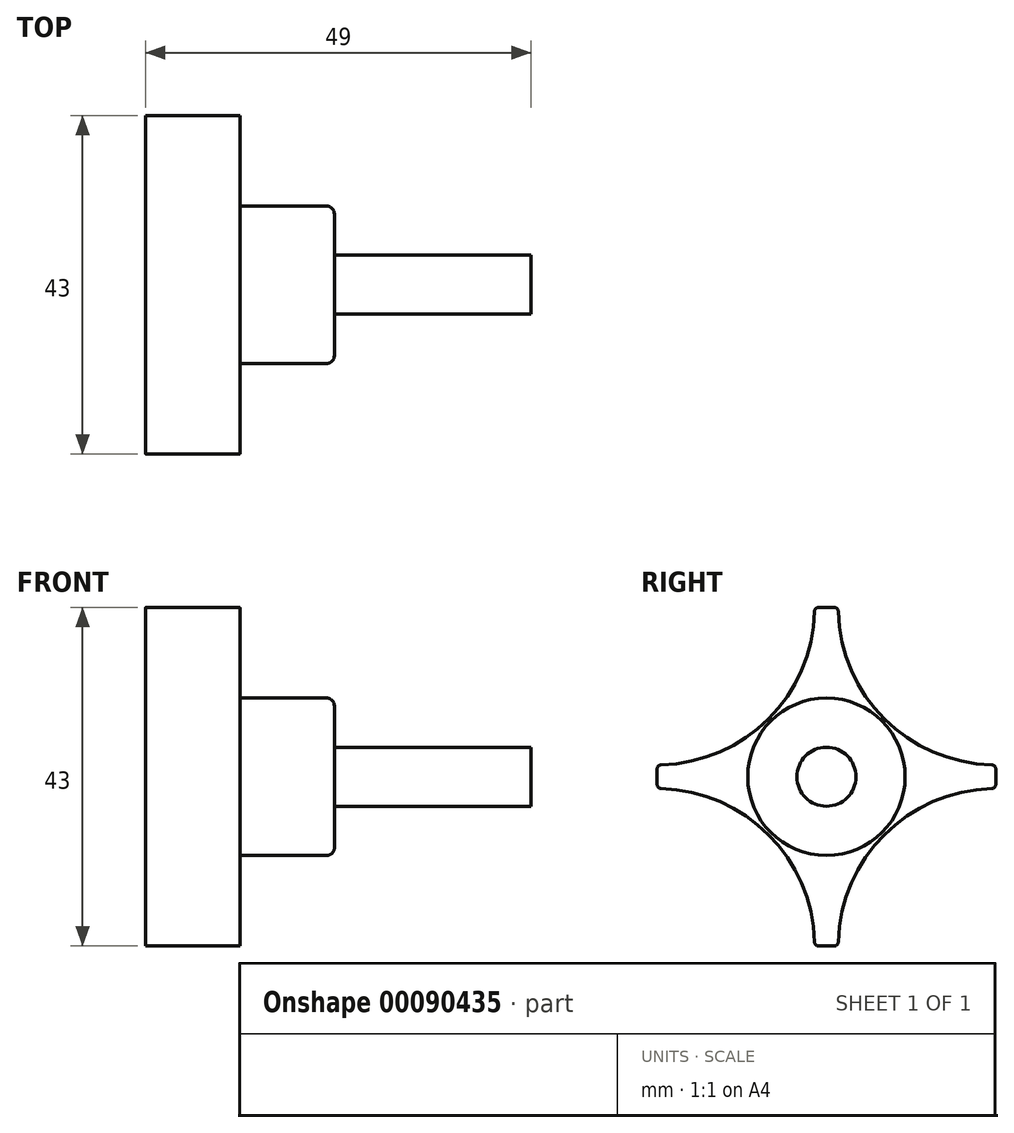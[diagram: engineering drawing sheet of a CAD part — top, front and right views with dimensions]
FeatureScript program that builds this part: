
annotation { "Feature Type Name" : "Feature", "Feature Type Description" : "" }
export const myFeature = defineFeature(function(context is Context, id is Id, definition is map)
    precondition{}
    {
        {
            var Q0;
            Q0=qCreatedBy(makeId("Right.planeOp"),FACE);
            var sketch = newSketch(context, id + "F0", { "sketchPlane" : qUnion([Q0])});
            skLineSegment(sketch, "E0.bottom", {"start": v(1.5, 21.5) * mm, "end": v(-1.5, 21.5) * mm});
            skLineSegment(sketch, "E0.top", {"start": v(1.5, -21.5) * mm, "end": v(-1.5, -21.5) * mm});
            skLineSegment(sketch, "E0.left", {"start": v(21.5, 1.5) * mm, "end": v(21.5, -1.5) * mm});
            skLineSegment(sketch, "E0.right", {"start": v(-21.5, 1.5) * mm, "end": v(-21.5, -1.5) * mm});
            skPoint(sketch, "E0.middle", {"position": v(0, 0) * mm});
            skArc(sketch, "E1", {"start": v(-1.5, 21.5) * mm, "mid": v(-7.36, 7.36) * mm, "end": v(-21.5, 1.5) * mm});
            skArc(sketch, "E2.MirrorCS", {"start": v(-1.5, -21.5) * mm, "mid": v(-7.36, -7.36) * mm, "end": v(-21.5, -1.5) * mm});
            skArc(sketch, "E3.MirrorCS", {"start": v(1.5, 21.5) * mm, "mid": v(7.36, 7.36) * mm, "end": v(21.5, 1.5) * mm});
            skArc(sketch, "E4.MirrorCS", {"start": v(1.5, -21.5) * mm, "mid": v(7.36, -7.36) * mm, "end": v(21.5, -1.5) * mm});
            skPoint(sketch, "E5", {"position": v(-21.5, 1.5) * mm});
            skPoint(sketch, "E6", {"position": v(-1.5, 21.5) * mm});
            skSolve(sketch);
        }
        {
            var Q0;
            {var subQ5=sQuery(id+"F0.wireOp",EDGE,"9f849e79-f11d-4500-882e-4ccdfb80906d0.MirrorC");var subQ12=sQuery(id+"F0.wireOp",EDGE,"E0.bottom");var subQ13=makeQuery(id+"F0.imprint","INTERSECT",VERTEX,{"derivedFrom":[subQ12,subQ5]});Q0=makeQuery(id+"F0.imprint","IMPRINT",FACE,{"disambiguationData":[TD([[makeQuery(id+"F0.imprint","IMPRINT",EDGE,{"disambiguationData":[TD([[subQ13,-1.0]])],"derivedFrom":subQ12}),1.0]])]});}
            extrude(context, id + "F1", {"entities" : qUnion([Q0]), "endBound" : BoundingType.SYMMETRIC, "depth" : 12 * mm});
        }
        {
            var Q0;
            Q0=makeQuery(id+"F1.opExtrude","CAP_FACE",FACE,{"disambiguationData":[OSD([sQuery(id+"F0.wireOp",EDGE,"E0.bottom"),sQuery(id+"F0.wireOp",EDGE,"E0.top"),sQuery(id+"F0.wireOp",EDGE,"E0.left"),sQuery(id+"F0.wireOp",EDGE,"E0.right"),sQuery(id+"F0.wireOp",EDGE,"AR0YrZLZ-1kNq-lMIp-wOmw-0kLK68b87y8J"),sQuery(id+"F0.wireOp",EDGE,"b24a8552-e674-496d-a4c2-55113b73f40c0.MirrorC"),sQuery(id+"F0.wireOp",EDGE,"0251b3db-de44-418e-883c-25e072dfbb100.MirrorC"),sQuery(id+"F0.wireOp",EDGE,"9f849e79-f11d-4500-882e-4ccdfb80906d0.MirrorC")])],"isStart":false});
            var sketch = newSketch(context, id + "F2", { "sketchPlane" : qUnion([Q0])});
            skCircle(sketch, "E7", {"center": v(0, 0) * mm, "radius": 10 * mm});
            skSolve(sketch);
        }
        {
            var Q0;
            Q0=makeQuery(id+"F1.opExtrude","SWEPT_EDGE",EDGE,{"disambiguationData":[OSD([sQuery(id+"F0.wireOp",EDGE,"E0.right"),sQuery(id+"F0.wireOp",EDGE,"E2.MirrorCS")])]});
            var Q1;
            Q1=makeQuery(id+"F1.opExtrude","SWEPT_EDGE",EDGE,{"disambiguationData":[OSD([sQuery(id+"F0.wireOp",EDGE,"E0.top"),sQuery(id+"F0.wireOp",EDGE,"E2.MirrorCS")])]});
            var Q2;
            Q2=makeQuery(id+"F1.opExtrude","SWEPT_EDGE",EDGE,{"disambiguationData":[OSD([sQuery(id+"F0.wireOp",EDGE,"E0.top"),sQuery(id+"F0.wireOp",EDGE,"E4.MirrorCS")])]});
            var Q3;
            Q3=makeQuery(id+"F1.opExtrude","SWEPT_EDGE",EDGE,{"disambiguationData":[OSD([sQuery(id+"F0.wireOp",EDGE,"E0.left"),sQuery(id+"F0.wireOp",EDGE,"E4.MirrorCS")])]});
            var Q4;
            Q4=makeQuery(id+"F1.opExtrude","SWEPT_EDGE",EDGE,{"disambiguationData":[OSD([sQuery(id+"F0.wireOp",EDGE,"E0.bottom"),sQuery(id+"F0.wireOp",EDGE,"E3.MirrorCS")])]});
            var Q5;
            Q5=makeQuery(id+"F1.opExtrude","SWEPT_EDGE",EDGE,{"disambiguationData":[OSD([sQuery(id+"F0.wireOp",EDGE,"E0.right"),sQuery(id+"F0.wireOp",EDGE,"E1")])]});
            var Q6;
            Q6=makeQuery(id+"F1.opExtrude","SWEPT_EDGE",EDGE,{"disambiguationData":[OSD([sQuery(id+"F0.wireOp",EDGE,"E0.bottom"),sQuery(id+"F0.wireOp",EDGE,"E1")])]});
            var Q7;
            Q7=makeQuery(id+"F1.opExtrude","SWEPT_EDGE",EDGE,{"disambiguationData":[OSD([sQuery(id+"F0.wireOp",EDGE,"E0.left"),sQuery(id+"F0.wireOp",EDGE,"E3.MirrorCS")])]});
            fillet(context, id + "F3", {"entities" : qUnion([Q0, Q1, Q2, Q3, Q4, Q5, Q6, Q7]), "radius" : .5 * mm, "tangentPropagation" : true, "allowEdgeOverflow" : false});
        }
        {
            var Q0;
            Q0 = qSketchRegion(id + "F2", true);
            extrude(context, id + "F4", {"entities" : qUnion([Q0]), "operationType" : NewBodyOperationType.ADD, "depth" : 12 * mm});
        }
        {
            var Q0;
            Q0=makeQuery(id+"F4.opExtrude","CAP_EDGE",EDGE,{"disambiguationData":[OSD([sQuery(id+"F2.wireOp",EDGE,"E7")])],"isStart":false});
            fillet(context, id + "F5", {"entities" : qUnion([Q0]), "radius" : 1 * mm, "tangentPropagation" : true, "allowEdgeOverflow" : false});
        }
        {
            var Q0;
            Q0=makeQuery(id+"F4.opExtrude","CAP_FACE",FACE,{"disambiguationData":[OSD([sQuery(id+"F2.wireOp",EDGE,"E7")])],"isStart":false});
            var sketch = newSketch(context, id + "F6", { "sketchPlane" : qUnion([Q0])});
            skCircle(sketch, "E8", {"center": v(0, 0) * mm, "radius": 3.75 * mm});
            skSolve(sketch);
        }
        {
            var Q0;
            Q0 = qSketchRegion(id + "F6", true);
            extrude(context, id + "F7", {"entities" : qUnion([Q0]), "operationType" : NewBodyOperationType.ADD, "depth" : 25 * mm});
        }
    });
